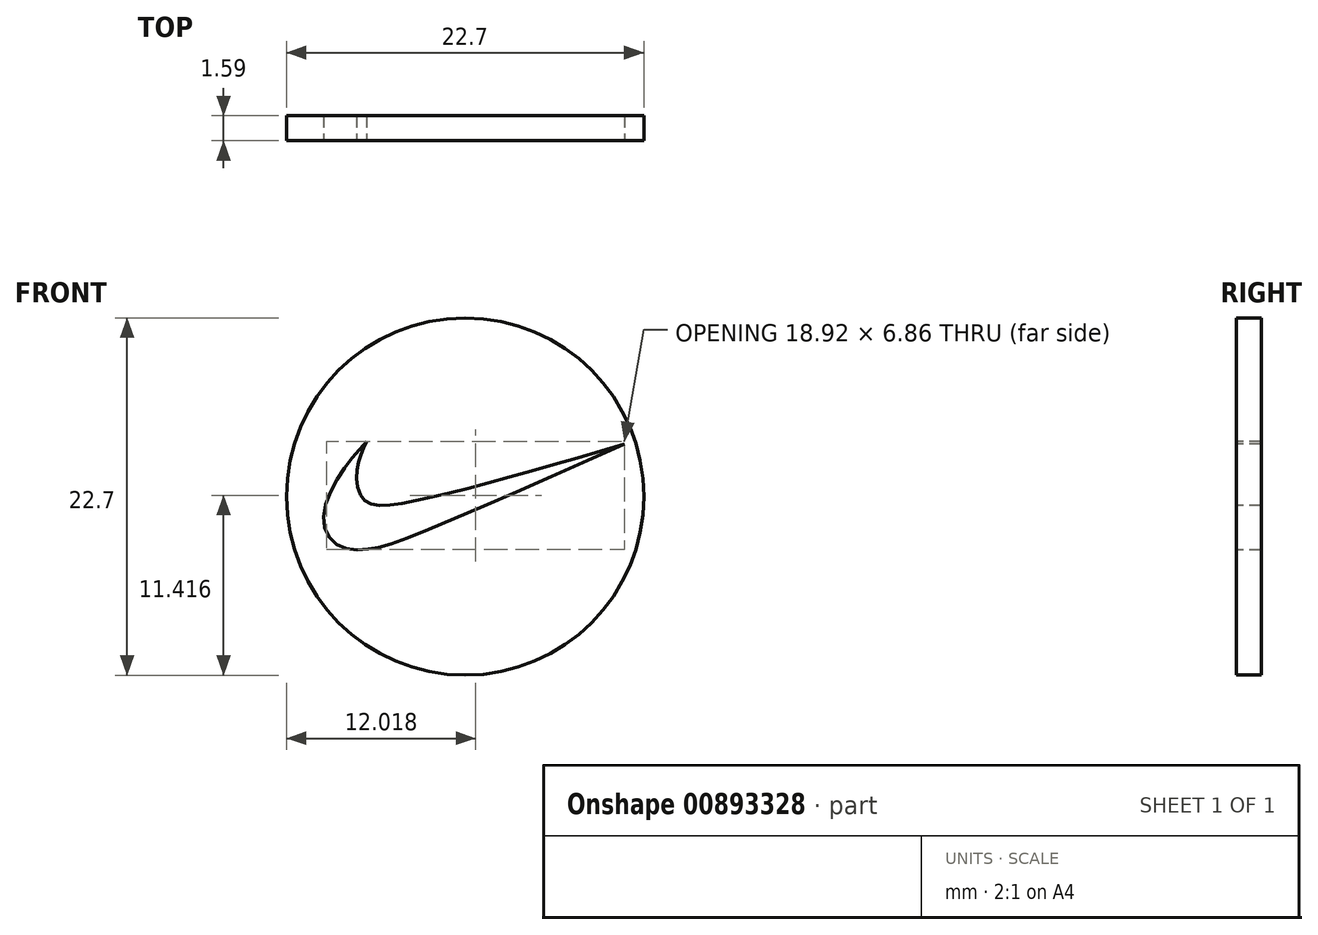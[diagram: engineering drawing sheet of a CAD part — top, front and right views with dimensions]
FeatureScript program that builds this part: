
annotation { "Feature Type Name" : "Feature", "Feature Type Description" : "" }
export const myFeature = defineFeature(function(context is Context, id is Id, definition is map)
    precondition{}
    {
        {
            var Q0;
            Q0=qCreatedBy(makeId("Front.planeOp"),FACE);
            var sketch = newSketch(context, id + "F0", { "sketchPlane" : qUnion([Q0])});
            skCircle(sketch, "E0", {"center": v(0, 0) * mm, "radius": 11.2 * mm, "construction": true});
            skFitSpline(sketch, "E1", {"points": [v(-6.11, 3.28) * mm, v(-6.6, 2.28) * mm, v(-6.85, 1.07) * mm, v(-6.76, 0.22) * mm, v(-6.15, -0.53) * mm, v(-5, -0.83) * mm, v(-2.93, -0.46) * mm, v(10.29, 3.1) * mm], "startDerivative": vector(-5.1, -9.3) * mm, "endDerivative": vector(44.83, 12.23) * mm});
            skFitSpline(sketch, "E2", {"points": [v(10.29, 3.1) * mm, v(-4.77, -3.38) * mm, v(-6.96, -3.64) * mm, v(-8.1, -3.38) * mm, v(-9, -1.91) * mm, v(-8.23, 0.72) * mm, v(-6.29, 2.96) * mm], "startDerivative": vector(-51.2, -23.98) * mm, "endDerivative": vector(13.8, 13.65) * mm});
            skCircle(sketch, "E3", {"center": v(0, -0.18) * mm, "radius": 11.35 * mm});
            skSolve(sketch);
        }
        {
            var Q0;
            Q0 = qSketchRegion(id + "F0", true);
            extrude(context, id + "F1", {"entities" : qUnion([Q0]), "depth" : 1.59 * mm, "offsetDistance" : 25.4 * mm});
        }
        {
            var Q0;
            Q0=makeQuery(id+"F1.opExtrude","CAP_FACE",FACE,{"disambiguationData":[OSD([sQuery(id+"F0.wireOp",EDGE,"E3")])],"isStart":false});
            var sketch = newSketch(context, id + "F2", { "sketchPlane" : qUnion([Q0])});
            skFitSpline(sketch, "E4", {"points": [v(-6.25, 3.32) * mm, v(-6.84, 1.68) * mm, v(-6.47, -0.34) * mm, v(-3.64, -0.54) * mm, v(10.13, 3.15) * mm], "startDerivative": vector(-4.57, -9.27) * mm, "endDerivative": vector(34.73, 10.16) * mm});
            skFitSpline(sketch, "E5", {"points": [v(10.13, 3.15) * mm, v(-4.06, -2.95) * mm, v(-6.29, -3.54) * mm, v(-7.94, -3.35) * mm, v(-8.92, -2.22) * mm, v(-8.73, -0.32) * mm, v(-7.43, 1.96) * mm, v(-6.25, 3.32) * mm], "startDerivative": vector(-54.2, -24.03) * mm, "endDerivative": vector(10.62, 11.33) * mm});
            skSolve(sketch);
        }
        {
            var Q0;
            Q0 = qSketchRegion(id + "F2", true);
            extrude(context, id + "F3", {"entities" : qUnion([Q0]), "operationType" : NewBodyOperationType.REMOVE, "oppositeDirection" : true, "depth" : 25.4 * mm, "offsetDistance" : 25.4 * mm});
        }
    });
